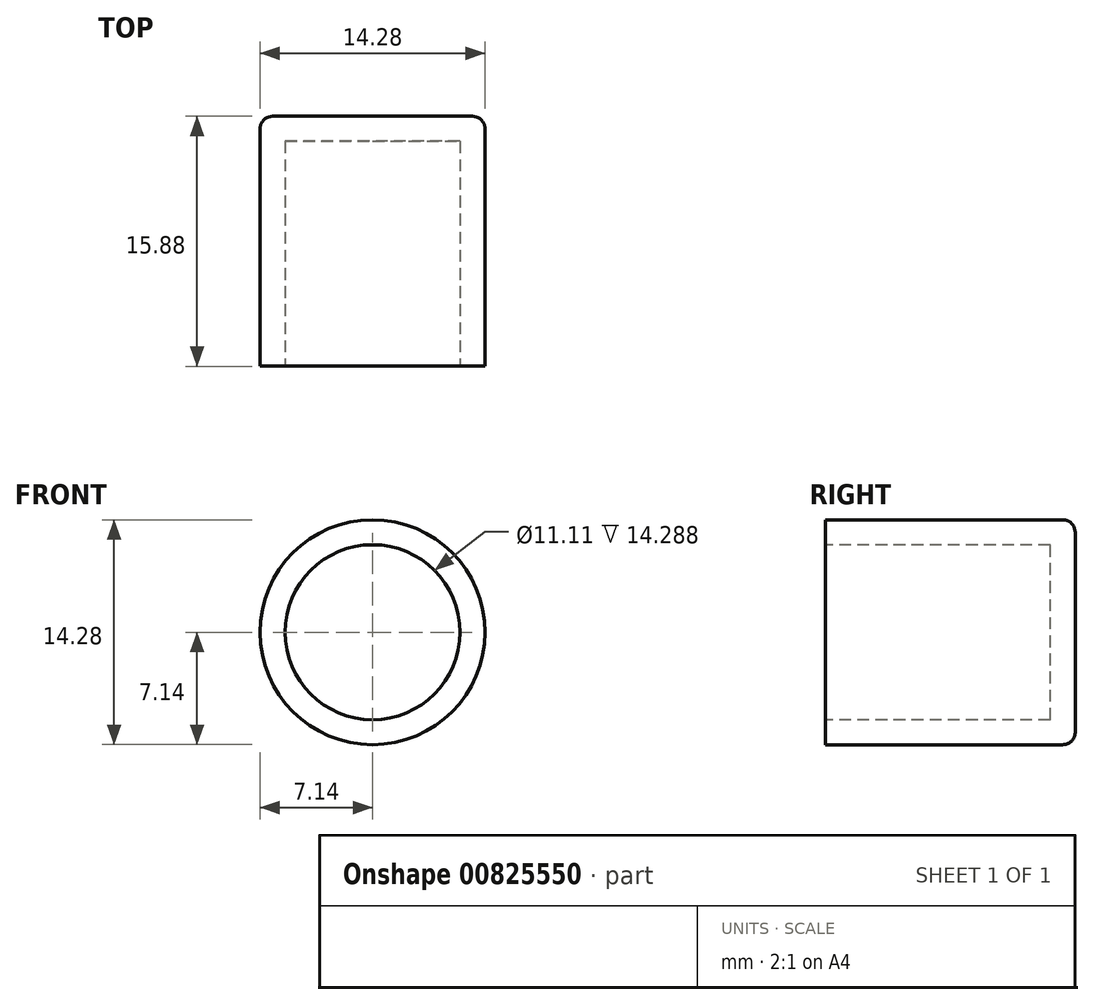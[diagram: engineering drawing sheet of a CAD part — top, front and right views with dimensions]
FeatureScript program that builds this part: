
annotation { "Feature Type Name" : "Feature", "Feature Type Description" : "" }
export const myFeature = defineFeature(function(context is Context, id is Id, definition is map)
    precondition{}
    {
        {
            var Q0;
            Q0=qCreatedBy(makeId("Top.planeOp"),FACE);
            var sketch = newSketch(context, id + "F0", { "sketchPlane" : qUnion([Q0])});
            skLineSegment(sketch, "E0.bottom", {"start": v(-7.14, -7.94) * mm, "end": v(-5.56, -7.94) * mm});
            skLineSegment(sketch, "E0.top", {"start": v(-6.35, 7.94) * mm, "end": v(0, 7.94) * mm});
            skLineSegment(sketch, "E0.left", {"start": v(-7.14, -7.94) * mm, "end": v(-7.14, 7.14) * mm});
            skPoint(sketch, "E0.middle", {"position": v(0, 0) * mm});
            skLineSegment(sketch, "E1.0", {"start": v(-5.56, -7.94) * mm, "end": v(-5.56, 6.35) * mm});
            skLineSegment(sketch, "E2.0", {"start": v(-5.56, 6.35) * mm, "end": v(0, 6.35) * mm});
            skLineSegment(sketch, "E3", {"start": v(0, 6.35) * mm, "end": v(0, 7.94) * mm});
            skPoint(sketch, "E3.endSnap0", {"position": v(0, 6.35) * mm});
            skPoint(sketch, "E4.visualSharp", {"position": v(-7.14, 7.94) * mm});
            skArc(sketch, "E4.filletArc", {"start": v(-6.35, 7.94) * mm, "mid": v(-6.91, 7.7) * mm, "end": v(-7.14, 7.14) * mm});
            skSolve(sketch);
        }
        {
            var Q0;
            Q0 = qSketchRegion(id + "F0", true);
            var Q1;
            Q1=sQuery(id+"F0.wireOp",EDGE,"E3");
            revolve(context, id + "F1", {"surfaceOperationType" : NewSurfaceOperationType.NEW, "entities" : qUnion([Q0]), "axis" : qUnion([Q1]), "revolveType" : RevolveType.FULL});
        }
    });
